# Revit family: Haworth_ComposeConnections_Panel_Solid
name_source: partatom
category: Furniture Systems
revit_build: Autodesk Revit 2018 (Build: 20170223_1515(x64)
units: mm (PartAtom-declared; Revit-internal decimal feet)

## family parameters
Always vertical = Yes
Cut with Voids When Loaded = No
OmniClass Number = 23.40.70.14.64.21
OmniClass Title = Systems Furniture
Part Type = Normal
Room Calculation Point = No
Round Connector Dimension = Use Diameter
Shared = No
Work Plane-Based = No

## types (9) — shared parameters
Actual Height = 25 1/2"
Assembly Code = E2020500
Bottom Trim Width = 1 1/2"
Custom Size = No
Description = Haworth - Compose Connections - Panel - Solid
Gap Offset = 1/4"
Height = 25 1/2"
Manufacturer = Haworth
Max. Width = 72"
Min. Width = 24"
Min/Max Height = 25.5 in.
Min/Max Width = 24-72 in. @ 6 in. Increments
Model = VZFS
Panel Depth = 1/2"
Revision Number = 3
Size = Verify Final Dim. w/ Haworth
Sustainability Info = http://media.haworth.com
Technology Trim Finish = Haworth _ Paint _ Gray Tone
Top Trim Width = 1/4"
Trim Depth = 3"
Trim Finish = Haworth _ Paint _ Gray Tone
URL = http://www.haworth.com
URL - Product = http://haworth.com
Warranty = https://www.haworth.com

## per-type parameters (varying)
| type | Actual Width | Panel Width | Width |
| 24w 25h | 24" | 24" | 24" |
| 30w 25h | 30" | 30" | 30" |
| 36w 25h | 36" | 36" | 36" |
| 42w 25h | 42" | 42" | 42" |
| 48w 25h | 48" | 48" | 48" |
| 54w 25h | 54" | 54" | 54" |
| 60w 25h | 60" | 60" | 60" |
| 66w 25h | 66" | 66" | 66" |
| 72w 25h | 72" | 72" | 72" |

## geometry (parser evidence)
native form markers: Sweep x8
no freeform markers — native parametric forms only
